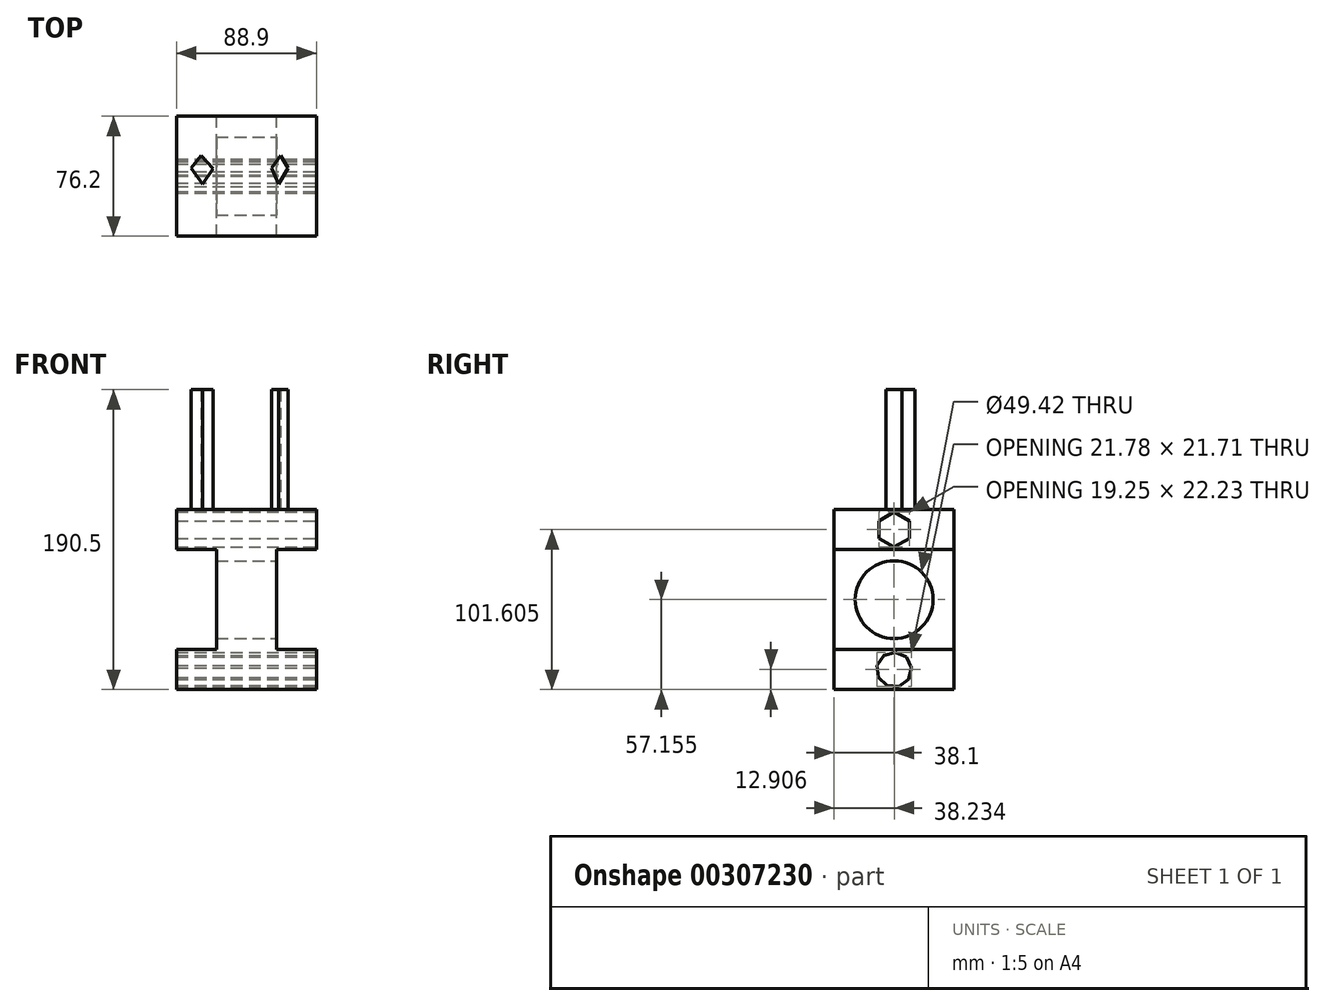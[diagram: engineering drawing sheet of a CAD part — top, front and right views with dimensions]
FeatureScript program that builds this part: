
annotation { "Feature Type Name" : "Feature", "Feature Type Description" : "" }
export const myFeature = defineFeature(function(context is Context, id is Id, definition is map)
    precondition{}
    {
        {
            var Q0;
            Q0=qCreatedBy(makeId("Front.planeOp"),FACE);
            var sketch = newSketch(context, id + "F0", { "sketchPlane" : qUnion([Q0])});
            skLineSegment(sketch, "E0", {"start": v(-46.75, -52.73) * mm, "end": v(42.15, -52.73) * mm});
            skLineSegment(sketch, "E1", {"start": v(42.15, -52.73) * mm, "end": v(42.15, -27.33) * mm});
            skLineSegment(sketch, "E2", {"start": v(42.15, -27.33) * mm, "end": v(16.75, -27.33) * mm});
            skLineSegment(sketch, "E3", {"start": v(16.75, -27.33) * mm, "end": v(16.75, 36.17) * mm});
            skLineSegment(sketch, "E4", {"start": v(16.75, 36.17) * mm, "end": v(42.15, 36.17) * mm});
            skLineSegment(sketch, "E5", {"start": v(42.15, 36.17) * mm, "end": v(42.15, 61.57) * mm});
            skLineSegment(sketch, "E6", {"start": v(42.15, 61.57) * mm, "end": v(-46.75, 61.57) * mm});
            skLineSegment(sketch, "E7", {"start": v(-46.75, 61.57) * mm, "end": v(-46.75, 36.17) * mm});
            skLineSegment(sketch, "E8", {"start": v(-46.75, 36.17) * mm, "end": v(-21.35, 36.17) * mm});
            skLineSegment(sketch, "E9", {"start": v(-21.35, 36.17) * mm, "end": v(-21.35, -27.33) * mm});
            skLineSegment(sketch, "E10", {"start": v(-21.35, -27.33) * mm, "end": v(-46.75, -27.33) * mm});
            skLineSegment(sketch, "E11", {"start": v(-46.75, -27.33) * mm, "end": v(-46.75, -52.73) * mm});
            skSolve(sketch);
        }
        {
            var Q0;
            Q0=makeQuery(id+"F0.imprint","IMPRINT",FACE,{"disambiguationData":[TD([[makeQuery(id+"F0.imprint","IMPRINT",EDGE,{"derivedFrom":sQuery(id+"F0.wireOp",EDGE,"E0")}),1.0]])]});
            extrude(context, id + "F1", {"entities" : qUnion([Q0]), "depth" : 76.2 * mm});
        }
        {
            var Q0;
            Q0=makeQuery(id+"F1.opExtrude","SWEPT_FACE",FACE,{"disambiguationData":[OSD([sQuery(id+"F0.wireOp",EDGE,"E3")])]});
            var sketch = newSketch(context, id + "F2", { "sketchPlane" : qUnion([Q0])});
            skCircle(sketch, "E12", {"center": v(-38.1, 4.42) * mm, "radius": 24.7 * mm});
            skPoint(sketch, "E12.centerSnap0", {"position": v(-76.2, 4.42) * mm});
            skPoint(sketch, "E12.centerSnap1", {"position": v(-38.1, 36.17) * mm});
            skSolve(sketch);
        }
        {
            var Q0;
            Q0=makeQuery(id+"F2.imprint","IMPRINT",FACE,{"disambiguationData":[TD([[makeQuery(id+"F2.imprint","IMPRINT",EDGE,{"derivedFrom":sQuery(id+"F2.wireOp",EDGE,"E12")}),1.0]])]});
            extrude(context, id + "F3", {"entities" : qUnion([Q0]), "operationType" : NewBodyOperationType.REMOVE, "endBound" : BoundingType.THROUGH_ALL, "oppositeDirection" : true, "depth" : 25.4 * mm});
        }
        {
            var Q0;
            Q0=makeQuery(id+"F1.opExtrude","SWEPT_FACE",FACE,{"disambiguationData":[OSD([sQuery(id+"F0.wireOp",EDGE,"E5")])]});
            var sketch = newSketch(context, id + "F4", { "sketchPlane" : qUnion([Q0])});
            skCircle(sketch, "E13.cCircle", {"center": v(-38.1, 48.87) * mm, "radius": 9.62 * mm, "construction": true});
            skPoint(sketch, "E13.cCircle.centerSnap0", {"position": v(-76.2, 48.87) * mm});
            skPoint(sketch, "E13.cCircle.centerSnap1", {"position": v(-38.1, 61.57) * mm});
            skLineSegment(sketch, "E13.0", {"start": v(-28.48, 54.43) * mm, "end": v(-28.48, 43.32) * mm});
            skLineSegment(sketch, "E13.1", {"start": v(-28.48, 43.32) * mm, "end": v(-38.1, 37.76) * mm});
            skLineSegment(sketch, "E13.2", {"start": v(-38.1, 37.76) * mm, "end": v(-47.72, 43.32) * mm});
            skLineSegment(sketch, "E13.3", {"start": v(-47.72, 43.32) * mm, "end": v(-47.72, 54.43) * mm});
            skLineSegment(sketch, "E13.4", {"start": v(-47.72, 54.43) * mm, "end": v(-38.1, 59.99) * mm});
            skLineSegment(sketch, "E13.5", {"start": v(-38.1, 59.99) * mm, "end": v(-28.48, 54.43) * mm});
            skPoint(sketch, "E13.0.midPoint", {"position": v(-28.48, 48.87) * mm});
            skSolve(sketch);
        }
        {
            var Q0;
            Q0=makeQuery(id+"F4.imprint","IMPRINT",FACE,{"disambiguationData":[TD([[makeQuery(id+"F4.imprint","IMPRINT",EDGE,{"derivedFrom":sQuery(id+"F4.wireOp",EDGE,"E13.0")}),-1.0]])]});
            extrude(context, id + "F5", {"entities" : qUnion([Q0]), "operationType" : NewBodyOperationType.REMOVE, "endBound" : BoundingType.THROUGH_ALL, "oppositeDirection" : true, "depth" : 25.4 * mm});
        }
        {
            var Q0;
            Q0=makeQuery(id+"F1.opExtrude","SWEPT_FACE",FACE,{"disambiguationData":[OSD([sQuery(id+"F0.wireOp",EDGE,"E1")])]});
            var sketch = newSketch(context, id + "F6", { "sketchPlane" : qUnion([Q0])});
            skCircle(sketch, "E14.cCircle", {"center": v(-38.1, -40.03) * mm, "radius": 10.42 * mm, "construction": true});
            skPoint(sketch, "E14.cCircle.centerSnap0", {"position": v(-76.2, -40.03) * mm});
            skPoint(sketch, "E14.cCircle.centerSnap1", {"position": v(-38.1, -27.33) * mm});
            skLineSegment(sketch, "E14.0", {"start": v(-48.86, -37.35) * mm, "end": v(-44.62, -31.06) * mm});
            skLineSegment(sketch, "E14.1", {"start": v(-44.62, -31.06) * mm, "end": v(-37.33, -28.97) * mm});
            skLineSegment(sketch, "E14.2", {"start": v(-37.33, -28.97) * mm, "end": v(-30.4, -32.05) * mm});
            skLineSegment(sketch, "E14.3", {"start": v(-30.4, -32.05) * mm, "end": v(-27.08, -38.86) * mm});
            skLineSegment(sketch, "E14.4", {"start": v(-27.08, -38.86) * mm, "end": v(-28.9, -46.22) * mm});
            skLineSegment(sketch, "E14.5", {"start": v(-28.9, -46.22) * mm, "end": v(-35.04, -50.68) * mm});
            skLineSegment(sketch, "E14.6", {"start": v(-35.04, -50.68) * mm, "end": v(-42.6, -50.15) * mm});
            skLineSegment(sketch, "E14.7", {"start": v(-42.6, -50.15) * mm, "end": v(-48.06, -44.89) * mm});
            skLineSegment(sketch, "E14.8", {"start": v(-48.06, -44.89) * mm, "end": v(-48.86, -37.35) * mm});
            skPoint(sketch, "E14.0.midPoint", {"position": v(-46.74, -34.2) * mm});
            skSolve(sketch);
        }
        {
            var Q0;
            Q0=makeQuery(id+"F6.imprint","IMPRINT",FACE,{"disambiguationData":[TD([[makeQuery(id+"F6.imprint","IMPRINT",EDGE,{"derivedFrom":sQuery(id+"F6.wireOp",EDGE,"E14.0")}),-1.0]])]});
            extrude(context, id + "F7", {"entities" : qUnion([Q0]), "operationType" : NewBodyOperationType.REMOVE, "endBound" : BoundingType.THROUGH_ALL, "oppositeDirection" : true, "depth" : 25.4 * mm});
        }
        {
            var Q0;
            Q0=makeQuery(id+"F1.opExtrude","SWEPT_FACE",FACE,{"disambiguationData":[OSD([sQuery(id+"F0.wireOp",EDGE,"E6")])]});
            var sketch = newSketch(context, id + "F8", { "sketchPlane" : qUnion([Q0])});
            skSolve(sketch);
        }
        {
            var Q0;
            {var subQ0=sQuery(id+"F0.wireOp",EDGE,"E6");Q0=makeQuery(id+"F8.imprint","IMPRINT",FACE,{"disambiguationData":[TD([[makeQuery(id+"F8.imprint","IMPRINT",EDGE,{"derivedFrom":makeQuery(id+"F1.opExtrude","CAP_EDGE",EDGE,{"disambiguationData":[OSD([subQ0])],"isStart":true})}),1.0]])]});}
            var sketch = newSketch(context, id + "F9", { "sketchPlane" : qUnion([Q0])});
            skLineSegment(sketch, "E15", {"start": v(-31.26, -24.92) * mm, "end": v(-37.45, -32.96) * mm});
            skLineSegment(sketch, "E16", {"start": v(-37.45, -32.96) * mm, "end": v(-30.02, -43.18) * mm});
            skLineSegment(sketch, "E17", {"start": v(-30.02, -43.18) * mm, "end": v(-23.21, -32.96) * mm});
            skLineSegment(sketch, "E18", {"start": v(-23.21, -33.58) * mm, "end": v(-31.26, -24.92) * mm});
            skLineSegment(sketch, "E19", {"start": v(19.5, -24.92) * mm, "end": v(13.62, -32.96) * mm});
            skLineSegment(sketch, "E20", {"start": v(13.62, -32.96) * mm, "end": v(18.26, -43.18) * mm});
            skLineSegment(sketch, "E21", {"start": v(18.26, -43.18) * mm, "end": v(24.14, -32.96) * mm});
            skLineSegment(sketch, "E22", {"start": v(24.14, -32.96) * mm, "end": v(19.5, -24.92) * mm});
            skSolve(sketch);
        }
        {
            var Q0;
            Q0 = qSketchRegion(id + "F9", true);
            extrude(context, id + "F10", {"entities" : qUnion([Q0]), "operationType" : NewBodyOperationType.ADD, "depth" : 76.2 * mm});
        }
    });
